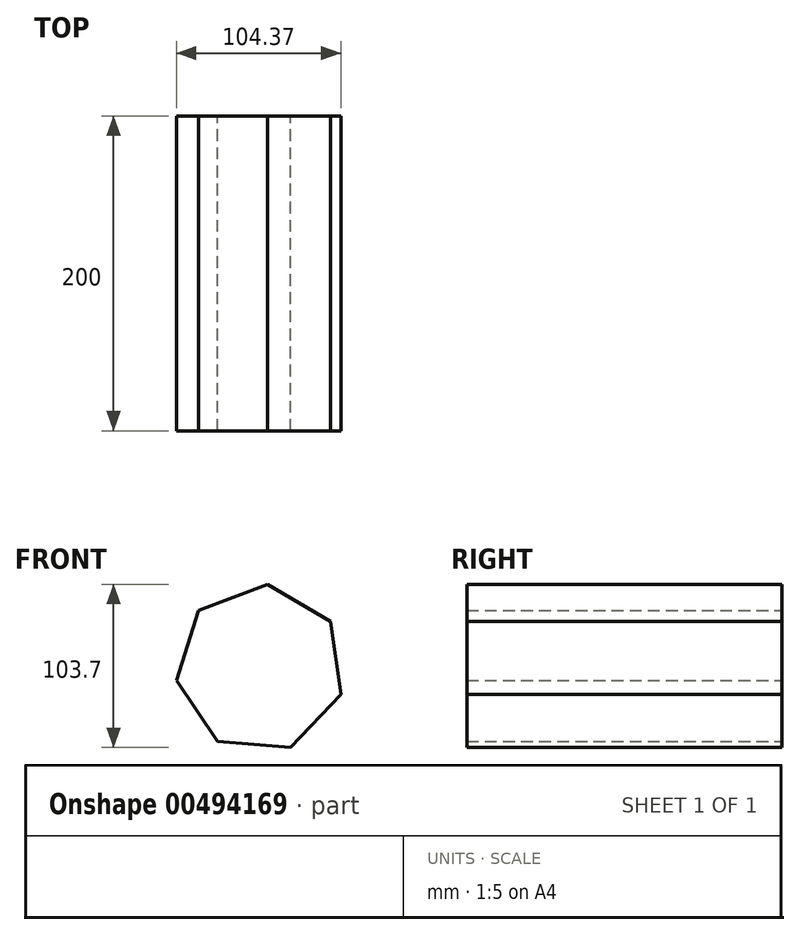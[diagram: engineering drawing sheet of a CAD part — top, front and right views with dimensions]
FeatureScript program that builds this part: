
annotation { "Feature Type Name" : "Feature", "Feature Type Description" : "" }
export const myFeature = defineFeature(function(context is Context, id is Id, definition is map)
    precondition{}
    {
        {
            var Q0;
            Q0=qCreatedBy(makeId("Front.planeOp"),FACE);
            var sketch = newSketch(context, id + "F0", { "sketchPlane" : qUnion([Q0])});
            skCircle(sketch, "E0.cCircle", {"center": v(0, 0) * mm, "radius": 53.71 * mm, "construction": true});
            skLineSegment(sketch, "E0.0", {"start": v(-39.06, 36.87) * mm, "end": v(4.48, 53.53) * mm});
            skLineSegment(sketch, "E0.1", {"start": v(4.48, 53.53) * mm, "end": v(44.64, 29.87) * mm});
            skLineSegment(sketch, "E0.2", {"start": v(44.64, 29.87) * mm, "end": v(51.19, -16.27) * mm});
            skLineSegment(sketch, "E0.3", {"start": v(51.19, -16.27) * mm, "end": v(19.2, -50.17) * mm});
            skLineSegment(sketch, "E0.4", {"start": v(19.2, -50.17) * mm, "end": v(-27.26, -46.28) * mm});
            skLineSegment(sketch, "E0.5", {"start": v(-27.26, -46.28) * mm, "end": v(-53.18, -7.55) * mm});
            skLineSegment(sketch, "E0.6", {"start": v(-53.18, -7.55) * mm, "end": v(-39.06, 36.87) * mm});
            skSolve(sketch);
        }
        {
            var Q0;
            Q0=makeQuery(id+"F0.imprint","IMPRINT",FACE,{"disambiguationData":[TD([[makeQuery(id+"F0.imprint","IMPRINT",EDGE,{"derivedFrom":sQuery(id+"F0.wireOp",EDGE,"E0.0")}),-1.0]])]});
            extrude(context, id + "F1", {"entities" : qUnion([Q0]), "endBound" : BoundingType.SYMMETRIC, "depth" : 200 * mm});
        }
    });
